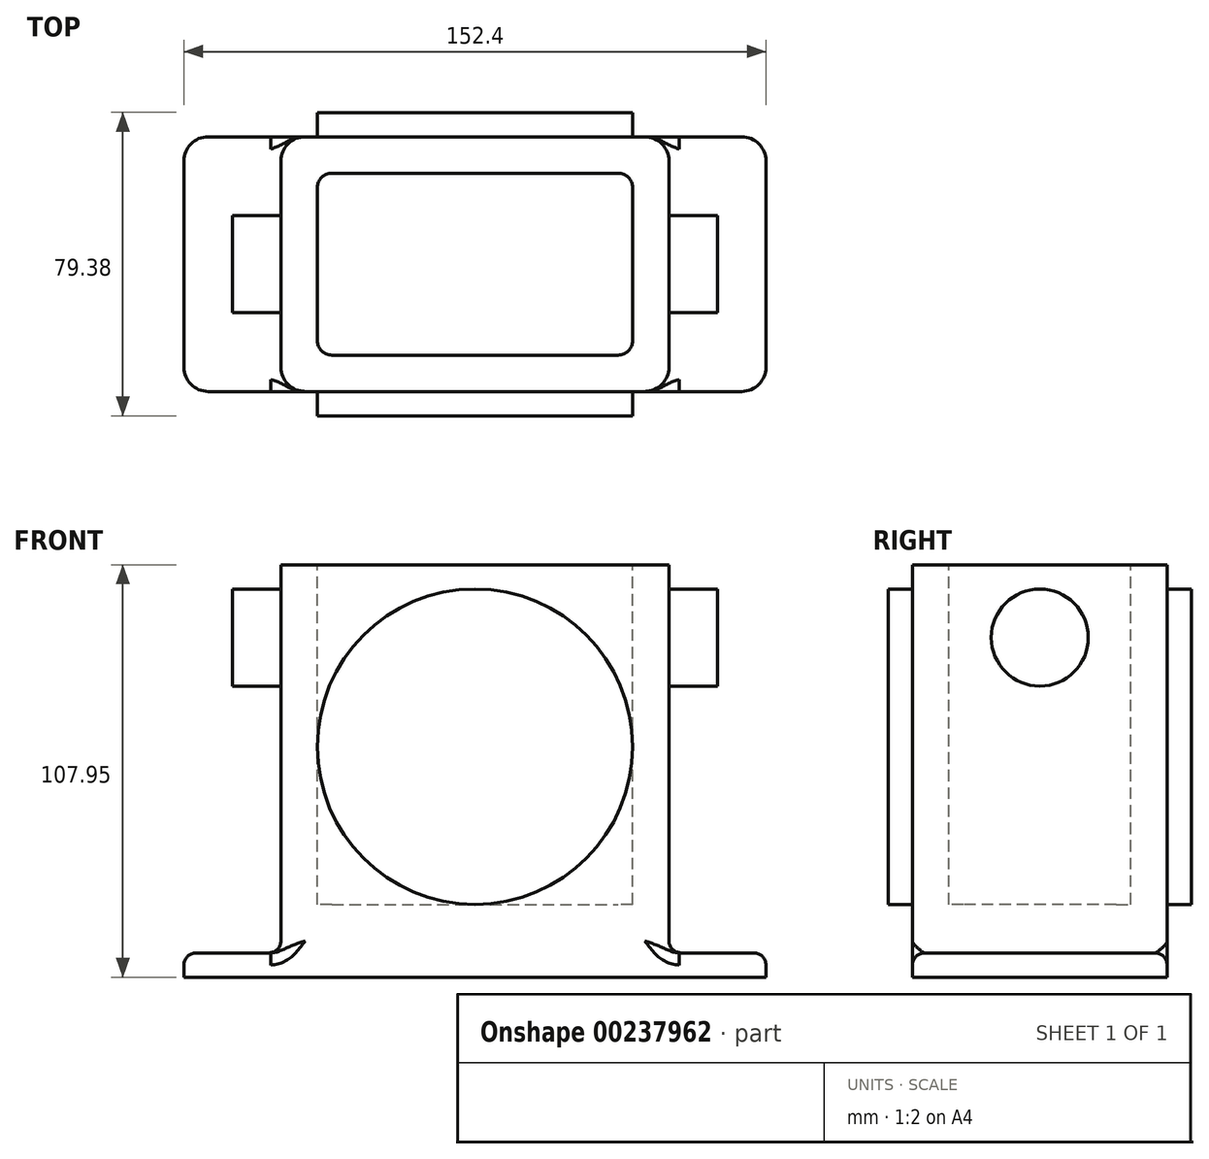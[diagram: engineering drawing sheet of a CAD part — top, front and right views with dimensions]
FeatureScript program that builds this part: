
annotation { "Feature Type Name" : "Feature", "Feature Type Description" : "" }
export const myFeature = defineFeature(function(context is Context, id is Id, definition is map)
    precondition{}
    {
        {
            var Q0;
            Q0=qCreatedBy(makeId("Top.planeOp"),FACE);
            var sketch = newSketch(context, id + "F0", { "sketchPlane" : qUnion([Q0])});
            skLineSegment(sketch, "E0.bottom", {"start": v(-76.2, 33.34) * mm, "end": v(76.2, 33.34) * mm});
            skLineSegment(sketch, "E0.top", {"start": v(-76.2, -33.34) * mm, "end": v(76.2, -33.34) * mm});
            skLineSegment(sketch, "E0.left", {"start": v(-76.2, 33.34) * mm, "end": v(-76.2, -33.34) * mm});
            skLineSegment(sketch, "E0.right", {"start": v(76.2, 33.34) * mm, "end": v(76.2, -33.34) * mm});
            skPoint(sketch, "E0.middle", {"position": v(0, 0) * mm});
            skSolve(sketch);
        }
        {
            var Q0;
            Q0 = qSketchRegion(id + "F0", true);
            extrude(context, id + "F1", {"entities" : qUnion([Q0]), "depth" : 6.35 * mm});
        }
        {
            var Q0;
            Q0=makeQuery(id+"F1.opExtrude","CAP_FACE",FACE,{"disambiguationData":[OSD([sQuery(id+"F0.wireOp",EDGE,"E0.bottom"),sQuery(id+"F0.wireOp",EDGE,"E0.top"),sQuery(id+"F0.wireOp",EDGE,"E0.left"),sQuery(id+"F0.wireOp",EDGE,"E0.right")])],"isStart":false});
            var sketch = newSketch(context, id + "F2", { "sketchPlane" : qUnion([Q0])});
            skLineSegment(sketch, "E1.bottom", {"start": v(-50.8, 33.34) * mm, "end": v(50.8, 33.34) * mm});
            skLineSegment(sketch, "E1.top", {"start": v(-50.8, -33.34) * mm, "end": v(50.8, -33.34) * mm});
            skLineSegment(sketch, "E1.left", {"start": v(-50.8, 33.34) * mm, "end": v(-50.8, -33.34) * mm});
            skLineSegment(sketch, "E1.right", {"start": v(50.8, 33.34) * mm, "end": v(50.8, -33.34) * mm});
            skPoint(sketch, "E1.middle", {"position": v(0, 0) * mm});
            skSolve(sketch);
        }
        {
            var Q0;
            Q0 = qSketchRegion(id + "F2", true);
            extrude(context, id + "F3", {"entities" : qUnion([Q0]), "operationType" : NewBodyOperationType.ADD, "depth" : 101.6 * mm});
        }
        {
            var Q0;
            Q0=makeQuery(id+"F3.opExtrude","SWEPT_EDGE",EDGE,{"disambiguationData":[OSD([sQuery(id+"F0.wireOp",EDGE,"E0.top"),sQuery(id+"F2.wireOp",EDGE,"E1.top"),sQuery(id+"F2.wireOp",EDGE,"E1.right")])]});
            var Q1;
            Q1=makeQuery(id+"F3.opExtrude","SWEPT_EDGE",EDGE,{"disambiguationData":[OSD([sQuery(id+"F0.wireOp",EDGE,"E0.top"),sQuery(id+"F2.wireOp",EDGE,"E1.top"),sQuery(id+"F2.wireOp",EDGE,"E1.left")])]});
            var Q2;
            Q2=makeQuery(id+"F3.opExtrude","SWEPT_EDGE",EDGE,{"disambiguationData":[OSD([sQuery(id+"F0.wireOp",EDGE,"E0.bottom"),sQuery(id+"F2.wireOp",EDGE,"E1.bottom"),sQuery(id+"F2.wireOp",EDGE,"E1.right")])]});
            var Q3;
            Q3=makeQuery(id+"F3.opExtrude","SWEPT_EDGE",EDGE,{"disambiguationData":[OSD([sQuery(id+"F0.wireOp",EDGE,"E0.bottom"),sQuery(id+"F2.wireOp",EDGE,"E1.bottom"),sQuery(id+"F2.wireOp",EDGE,"E1.left")])]});
            var Q4;
            Q4=makeQuery(id+"F1.opExtrude","SWEPT_EDGE",EDGE,{"disambiguationData":[OSD([sQuery(id+"F0.wireOp",EDGE,"E0.bottom"),sQuery(id+"F0.wireOp",EDGE,"E0.left")])]});
            var Q5;
            Q5=makeQuery(id+"F1.opExtrude","SWEPT_EDGE",EDGE,{"disambiguationData":[OSD([sQuery(id+"F0.wireOp",EDGE,"E0.bottom"),sQuery(id+"F0.wireOp",EDGE,"E0.right")])]});
            var Q6;
            Q6=makeQuery(id+"F1.opExtrude","SWEPT_EDGE",EDGE,{"disambiguationData":[OSD([sQuery(id+"F0.wireOp",EDGE,"E0.top"),sQuery(id+"F0.wireOp",EDGE,"E0.left")])]});
            var Q7;
            Q7=makeQuery(id+"F1.opExtrude","SWEPT_EDGE",EDGE,{"disambiguationData":[OSD([sQuery(id+"F0.wireOp",EDGE,"E0.top"),sQuery(id+"F0.wireOp",EDGE,"E0.right")])]});
            fillet(context, id + "F4", {"entities" : qUnion([Q0, Q1, Q2, Q3, Q4, Q5, Q6, Q7]), "radius" : 6.35 * mm, "tangentPropagation" : true, "allowEdgeOverflow" : false});
        }
        {
            var Q0;
            {var subQ0=sQuery(id+"F0.wireOp",EDGE,"E0.left");var subQ1=sQuery(id+"F0.wireOp",EDGE,"E0.top");var subQ2=sQuery(id+"F0.wireOp",EDGE,"E0.bottom");Q0=makeQuery(id+"F3.boolean.opBoolean","SPLIT",FACE,{"disambiguationData":[TD([makeQuery(id+"F1.opExtrude","SWEPT_FACE",FACE,{"disambiguationData":[OSD([subQ0])]})])],"derivedFrom":makeQuery(id+"F1.opExtrude","CAP_FACE",FACE,{"disambiguationData":[OSD([subQ2,subQ1,subQ0,sQuery(id+"F0.wireOp",EDGE,"E0.right")])],"isStart":false})});}
            var Q1;
            {var subQ0=sQuery(id+"F0.wireOp",EDGE,"E0.right");var subQ1=sQuery(id+"F0.wireOp",EDGE,"E0.top");var subQ2=sQuery(id+"F0.wireOp",EDGE,"E0.bottom");Q1=makeQuery(id+"F3.boolean.opBoolean","SPLIT",FACE,{"disambiguationData":[TD([makeQuery(id+"F1.opExtrude","SWEPT_FACE",FACE,{"disambiguationData":[OSD([subQ0])]})])],"derivedFrom":makeQuery(id+"F1.opExtrude","CAP_FACE",FACE,{"disambiguationData":[OSD([subQ2,subQ1,sQuery(id+"F0.wireOp",EDGE,"E0.left"),subQ0])],"isStart":false})});}
            fillet(context, id + "F5", {"entities" : qUnion([Q0, Q1]), "radius" : 3.17 * mm, "tangentPropagation" : true, "allowEdgeOverflow" : false});
        }
        {
            var Q0;
            Q0=makeQuery(id+"F3.opExtrude","CAP_FACE",FACE,{"disambiguationData":[OSD([sQuery(id+"F2.wireOp",EDGE,"E1.bottom"),sQuery(id+"F2.wireOp",EDGE,"E1.top"),sQuery(id+"F2.wireOp",EDGE,"E1.left"),sQuery(id+"F2.wireOp",EDGE,"E1.right")])],"isStart":false});
            var sketch = newSketch(context, id + "F6", { "sketchPlane" : qUnion([Q0])});
            skLineSegment(sketch, "E2.bottom", {"start": v(-37.47, 23.81) * mm, "end": v(37.46, 23.81) * mm});
            skLineSegment(sketch, "E2.top", {"start": v(-37.47, -23.81) * mm, "end": v(37.46, -23.81) * mm});
            skLineSegment(sketch, "E2.left", {"start": v(-41.28, 20) * mm, "end": v(-41.28, -20) * mm});
            skLineSegment(sketch, "E2.right", {"start": v(41.27, 20) * mm, "end": v(41.27, -20) * mm});
            skPoint(sketch, "E2.middle", {"position": v(0, 0) * mm});
            skPoint(sketch, "E3.visualSharp", {"position": v(-41.27, 23.81) * mm});
            skArc(sketch, "E3.filletArc", {"start": v(-37.47, 23.81) * mm, "mid": v(-40.16, 22.7) * mm, "end": v(-41.28, 20) * mm});
            skPoint(sketch, "E4.visualSharp", {"position": v(41.28, -23.81) * mm});
            skArc(sketch, "E4.filletArc", {"start": v(37.46, -23.81) * mm, "mid": v(40.16, -22.7) * mm, "end": v(41.28, -20) * mm});
            skPoint(sketch, "E5.visualSharp", {"position": v(41.28, 23.81) * mm});
            skArc(sketch, "E5.filletArc", {"start": v(41.27, 20) * mm, "mid": v(40.16, 22.7) * mm, "end": v(37.46, 23.81) * mm});
            skPoint(sketch, "E6.visualSharp", {"position": v(-41.27, -23.81) * mm});
            skArc(sketch, "E6.filletArc", {"start": v(-41.28, -20) * mm, "mid": v(-40.16, -22.7) * mm, "end": v(-37.47, -23.81) * mm});
            skSolve(sketch);
        }
        {
            var Q0;
            Q0 = qSketchRegion(id + "F6", true);
            extrude(context, id + "F7", {"entities" : qUnion([Q0]), "operationType" : NewBodyOperationType.REMOVE, "oppositeDirection" : true, "depth" : 88.9 * mm});
        }
        {
            var Q0;
            Q0=makeQuery(id+"F3.boolean.opBoolean","MERGE",FACE,{"derivedFrom":[makeQuery(id+"F1.opExtrude","SWEPT_FACE",FACE,{"disambiguationData":[OSD([sQuery(id+"F0.wireOp",EDGE,"E0.top")])]}),makeQuery(id+"F3.opExtrude","SWEPT_FACE",FACE,{"disambiguationData":[OSD([sQuery(id+"F2.wireOp",EDGE,"E1.top")])]})]});
            var sketch = newSketch(context, id + "F8", { "sketchPlane" : qUnion([Q0])});
            skCircle(sketch, "E7", {"center": v(0, 60.32) * mm, "radius": 41.28 * mm});
            skSolve(sketch);
        }
        {
            var Q0;
            Q0=makeQuery(id+"F8.imprint","IMPRINT",FACE,{"disambiguationData":[TD([[makeQuery(id+"F8.imprint","IMPRINT",EDGE,{"derivedFrom":sQuery(id+"F8.wireOp",EDGE,"E7")}),1.0]])]});
            extrude(context, id + "F9", {"entities" : qUnion([Q0]), "operationType" : NewBodyOperationType.ADD, "depth" : 6.35 * mm});
        }
        {
            var Q0;
            Q0=makeQuery(id+"F3.boolean.opBoolean","MERGE",FACE,{"derivedFrom":[makeQuery(id+"F1.opExtrude","SWEPT_FACE",FACE,{"disambiguationData":[OSD([sQuery(id+"F0.wireOp",EDGE,"E0.bottom")])]}),makeQuery(id+"F3.opExtrude","SWEPT_FACE",FACE,{"disambiguationData":[OSD([sQuery(id+"F2.wireOp",EDGE,"E1.bottom")])]})]});
            var sketch = newSketch(context, id + "F10", { "sketchPlane" : qUnion([Q0])});
            skCircle(sketch, "E8", {"center": v(0, 60.32) * mm, "radius": 41.28 * mm});
            skSolve(sketch);
        }
        {
            var Q0;
            Q0 = qSketchRegion(id + "F10", true);
            extrude(context, id + "F11", {"entities" : qUnion([Q0]), "operationType" : NewBodyOperationType.ADD, "depth" : 6.35 * mm});
        }
        {
            var Q0;
            Q0=makeQuery(id+"F3.opExtrude","SWEPT_FACE",FACE,{"disambiguationData":[OSD([sQuery(id+"F2.wireOp",EDGE,"E1.left")])]});
            var sketch = newSketch(context, id + "F12", { "sketchPlane" : qUnion([Q0])});
            skCircle(sketch, "E9", {"center": v(0, 88.9) * mm, "radius": 12.7 * mm});
            skSolve(sketch);
        }
        {
            var Q0;
            Q0 = qSketchRegion(id + "F12", true);
            extrude(context, id + "F13", {"entities" : qUnion([Q0]), "operationType" : NewBodyOperationType.ADD, "depth" : 12.7 * mm});
        }
        {
            var Q0;
            Q0=makeQuery(id+"F3.opExtrude","SWEPT_FACE",FACE,{"disambiguationData":[OSD([sQuery(id+"F2.wireOp",EDGE,"E1.right")])]});
            var sketch = newSketch(context, id + "F14", { "sketchPlane" : qUnion([Q0])});
            skCircle(sketch, "E10", {"center": v(0, 88.9) * mm, "radius": 12.7 * mm});
            skSolve(sketch);
        }
        {
            var Q0;
            Q0 = qSketchRegion(id + "F14", true);
            extrude(context, id + "F15", {"entities" : qUnion([Q0]), "operationType" : NewBodyOperationType.ADD, "depth" : 12.7 * mm});
        }
    });
